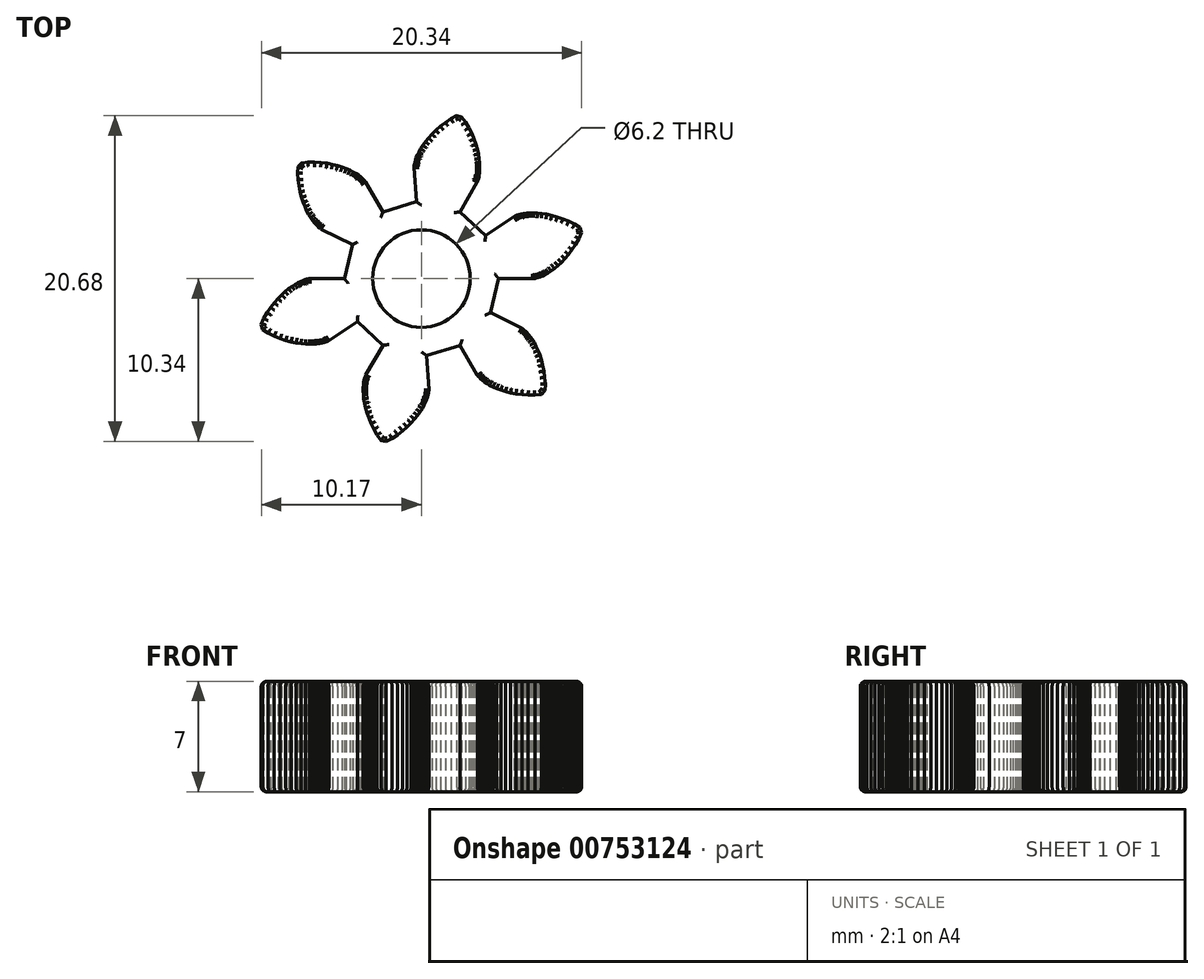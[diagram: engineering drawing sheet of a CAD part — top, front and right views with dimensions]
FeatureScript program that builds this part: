
annotation { "Feature Type Name" : "Feature", "Feature Type Description" : "" }
export const myFeature = defineFeature(function(context is Context, id is Id, definition is map)
    precondition{}
    {
        {
            var Q0;
            Q0=qCreatedBy(makeId("Top.planeOp"),FACE);
            var sketch = newSketch(context, id + "F0", { "sketchPlane" : qUnion([Q0])});
            skLineSegment(sketch, "E0", {"start": v(4.9, 0) * mm, "end": v(7.07, 0) * mm});
            skLineSegment(sketch, "E1", {"start": v(7.07, 0) * mm, "end": v(7.1, 0) * mm});
            skLineSegment(sketch, "E2", {"start": v(7.1, 0) * mm, "end": v(7.14, 0) * mm});
            skLineSegment(sketch, "E3", {"start": v(7.14, 0) * mm, "end": v(7.2, 0.02) * mm});
            skLineSegment(sketch, "E4", {"start": v(7.2, 0.02) * mm, "end": v(7.29, 0.04) * mm});
            skLineSegment(sketch, "E5", {"start": v(7.29, 0.04) * mm, "end": v(7.4, 0.07) * mm});
            skLineSegment(sketch, "E6", {"start": v(7.4, 0.07) * mm, "end": v(7.53, 0.11) * mm});
            skLineSegment(sketch, "E7", {"start": v(7.53, 0.11) * mm, "end": v(7.68, 0.18) * mm});
            skLineSegment(sketch, "E8", {"start": v(7.68, 0.18) * mm, "end": v(7.85, 0.26) * mm});
            skLineSegment(sketch, "E9", {"start": v(7.85, 0.26) * mm, "end": v(8.03, 0.36) * mm});
            skLineSegment(sketch, "E10", {"start": v(8.03, 0.36) * mm, "end": v(8.23, 0.49) * mm});
            skLineSegment(sketch, "E11", {"start": v(8.23, 0.49) * mm, "end": v(8.44, 0.64) * mm});
            skLineSegment(sketch, "E12", {"start": v(8.44, 0.64) * mm, "end": v(8.66, 0.82) * mm});
            skLineSegment(sketch, "E13", {"start": v(8.66, 0.82) * mm, "end": v(8.88, 1.03) * mm});
            skLineSegment(sketch, "E14", {"start": v(8.88, 1.03) * mm, "end": v(9.11, 1.27) * mm});
            skLineSegment(sketch, "E15", {"start": v(9.11, 1.27) * mm, "end": v(9.34, 1.54) * mm});
            skLineSegment(sketch, "E16", {"start": v(9.34, 1.54) * mm, "end": v(9.57, 1.84) * mm});
            skLineSegment(sketch, "E17", {"start": v(9.57, 1.84) * mm, "end": v(9.8, 2.17) * mm});
            skLineSegment(sketch, "E18", {"start": v(9.8, 2.17) * mm, "end": v(10.01, 2.54) * mm});
            skLineSegment(sketch, "E19", {"start": v(10.01, 2.54) * mm, "end": v(10.17, 2.92) * mm});
            skLineSegment(sketch, "E20", {"start": v(10.17, 2.92) * mm, "end": v(10.08, 3.23) * mm});
            skLineSegment(sketch, "E21", {"start": v(10.08, 3.23) * mm, "end": v(9.73, 3.46) * mm});
            skLineSegment(sketch, "E22", {"start": v(9.73, 3.46) * mm, "end": v(9.35, 3.64) * mm});
            skLineSegment(sketch, "E23", {"start": v(9.35, 3.64) * mm, "end": v(8.98, 3.8) * mm});
            skLineSegment(sketch, "E24", {"start": v(8.98, 3.8) * mm, "end": v(8.62, 3.92) * mm});
            skLineSegment(sketch, "E25", {"start": v(8.62, 3.92) * mm, "end": v(8.28, 4.02) * mm});
            skLineSegment(sketch, "E26", {"start": v(8.28, 4.02) * mm, "end": v(7.95, 4.08) * mm});
            skLineSegment(sketch, "E27", {"start": v(7.95, 4.08) * mm, "end": v(7.65, 4.13) * mm});
            skLineSegment(sketch, "E28", {"start": v(7.65, 4.13) * mm, "end": v(7.37, 4.16) * mm});
            skLineSegment(sketch, "E29", {"start": v(7.37, 4.16) * mm, "end": v(7.11, 4.17) * mm});
            skLineSegment(sketch, "E30", {"start": v(7.11, 4.17) * mm, "end": v(6.88, 4.17) * mm});
            skLineSegment(sketch, "E31", {"start": v(6.88, 4.17) * mm, "end": v(6.67, 4.15) * mm});
            skLineSegment(sketch, "E32", {"start": v(6.67, 4.15) * mm, "end": v(6.48, 4.12) * mm});
            skLineSegment(sketch, "E33", {"start": v(6.48, 4.12) * mm, "end": v(6.32, 4.1) * mm});
            skLineSegment(sketch, "E34", {"start": v(6.32, 4.1) * mm, "end": v(6.19, 4.06) * mm});
            skLineSegment(sketch, "E35", {"start": v(6.19, 4.06) * mm, "end": v(6.08, 4.02) * mm});
            skLineSegment(sketch, "E36", {"start": v(6.08, 4.02) * mm, "end": v(6, 4) * mm});
            skLineSegment(sketch, "E37", {"start": v(6, 4) * mm, "end": v(5.93, 3.96) * mm});
            skLineSegment(sketch, "E38", {"start": v(5.93, 3.96) * mm, "end": v(5.9, 3.94) * mm});
            skLineSegment(sketch, "E39", {"start": v(5.9, 3.94) * mm, "end": v(5.88, 3.93) * mm});
            skLineSegment(sketch, "E40", {"start": v(5.88, 3.93) * mm, "end": v(4.07, 2.72) * mm});
            skLineSegment(sketch, "E41", {"start": v(4.07, 2.72) * mm, "end": v(2.45, 4.24) * mm});
            skLineSegment(sketch, "E42", {"start": v(2.45, 4.24) * mm, "end": v(3.54, 6.13) * mm});
            skLineSegment(sketch, "E43", {"start": v(3.54, 6.13) * mm, "end": v(3.55, 6.14) * mm});
            skLineSegment(sketch, "E44", {"start": v(3.55, 6.14) * mm, "end": v(3.56, 6.18) * mm});
            skLineSegment(sketch, "E45", {"start": v(3.56, 6.18) * mm, "end": v(3.59, 6.25) * mm});
            skLineSegment(sketch, "E46", {"start": v(3.59, 6.25) * mm, "end": v(3.61, 6.33) * mm});
            skLineSegment(sketch, "E47", {"start": v(3.61, 6.33) * mm, "end": v(3.64, 6.44) * mm});
            skLineSegment(sketch, "E48", {"start": v(3.64, 6.44) * mm, "end": v(3.67, 6.58) * mm});
            skLineSegment(sketch, "E49", {"start": v(3.67, 6.58) * mm, "end": v(3.69, 6.74) * mm});
            skLineSegment(sketch, "E50", {"start": v(3.69, 6.74) * mm, "end": v(3.7, 6.93) * mm});
            skLineSegment(sketch, "E51", {"start": v(3.7, 6.93) * mm, "end": v(3.7, 7.14) * mm});
            skLineSegment(sketch, "E52", {"start": v(3.7, 7.14) * mm, "end": v(3.7, 7.37) * mm});
            skLineSegment(sketch, "E53", {"start": v(3.7, 7.37) * mm, "end": v(3.66, 7.63) * mm});
            skLineSegment(sketch, "E54", {"start": v(3.66, 7.63) * mm, "end": v(3.62, 7.9) * mm});
            skLineSegment(sketch, "E55", {"start": v(3.62, 7.9) * mm, "end": v(3.55, 8.2) * mm});
            skLineSegment(sketch, "E56", {"start": v(3.55, 8.2) * mm, "end": v(3.46, 8.52) * mm});
            skLineSegment(sketch, "E57", {"start": v(3.46, 8.52) * mm, "end": v(3.34, 8.86) * mm});
            skLineSegment(sketch, "E58", {"start": v(3.34, 8.86) * mm, "end": v(3.2, 9.2) * mm});
            skLineSegment(sketch, "E59", {"start": v(3.2, 9.2) * mm, "end": v(3.02, 9.57) * mm});
            skLineSegment(sketch, "E60", {"start": v(3.02, 9.57) * mm, "end": v(2.81, 9.94) * mm});
            skLineSegment(sketch, "E61", {"start": v(2.81, 9.94) * mm, "end": v(2.56, 10.27) * mm});
            skLineSegment(sketch, "E62", {"start": v(2.56, 10.27) * mm, "end": v(2.24, 10.34) * mm});
            skLineSegment(sketch, "E63", {"start": v(2.24, 10.34) * mm, "end": v(1.87, 10.16) * mm});
            skLineSegment(sketch, "E64", {"start": v(1.87, 10.16) * mm, "end": v(1.52, 9.92) * mm});
            skLineSegment(sketch, "E65", {"start": v(1.52, 9.92) * mm, "end": v(1.2, 9.67) * mm});
            skLineSegment(sketch, "E66", {"start": v(1.2, 9.67) * mm, "end": v(0.92, 9.42) * mm});
            skLineSegment(sketch, "E67", {"start": v(0.92, 9.42) * mm, "end": v(0.66, 9.18) * mm});
            skLineSegment(sketch, "E68", {"start": v(0.66, 9.18) * mm, "end": v(0.44, 8.93) * mm});
            skLineSegment(sketch, "E69", {"start": v(0.44, 8.93) * mm, "end": v(0.25, 8.7) * mm});
            skLineSegment(sketch, "E70", {"start": v(0.25, 8.7) * mm, "end": v(0.08, 8.46) * mm});
            skLineSegment(sketch, "E71", {"start": v(0.08, 8.46) * mm, "end": v(-0.06, 8.24) * mm});
            skLineSegment(sketch, "E72", {"start": v(-0.06, 8.24) * mm, "end": v(-0.17, 8.04) * mm});
            skLineSegment(sketch, "E73", {"start": v(-0.17, 8.04) * mm, "end": v(-0.26, 7.85) * mm});
            skLineSegment(sketch, "E74", {"start": v(-0.26, 7.85) * mm, "end": v(-0.33, 7.68) * mm});
            skLineSegment(sketch, "E75", {"start": v(-0.33, 7.68) * mm, "end": v(-0.38, 7.52) * mm});
            skLineSegment(sketch, "E76", {"start": v(-0.38, 7.52) * mm, "end": v(-0.42, 7.39) * mm});
            skLineSegment(sketch, "E77", {"start": v(-0.42, 7.39) * mm, "end": v(-0.45, 7.28) * mm});
            skLineSegment(sketch, "E78", {"start": v(-0.45, 7.28) * mm, "end": v(-0.46, 7.19) * mm});
            skLineSegment(sketch, "E79", {"start": v(-0.46, 7.19) * mm, "end": v(-0.47, 7.12) * mm});
            skLineSegment(sketch, "E80", {"start": v(-0.47, 7.12) * mm, "end": v(-0.47, 7.08) * mm});
            skLineSegment(sketch, "E81", {"start": v(-0.47, 7.08) * mm, "end": v(-0.47, 7.06) * mm});
            skLineSegment(sketch, "E82", {"start": v(-0.47, 7.06) * mm, "end": v(-0.32, 4.88) * mm});
            skLineSegment(sketch, "E83", {"start": v(-0.32, 4.88) * mm, "end": v(-2.45, 4.24) * mm});
            skLineSegment(sketch, "E84", {"start": v(-2.45, 4.24) * mm, "end": v(-3.54, 6.13) * mm});
            skLineSegment(sketch, "E85", {"start": v(-3.54, 6.13) * mm, "end": v(-3.55, 6.14) * mm});
            skLineSegment(sketch, "E86", {"start": v(-3.55, 6.14) * mm, "end": v(-3.57, 6.18) * mm});
            skLineSegment(sketch, "E87", {"start": v(-3.57, 6.18) * mm, "end": v(-3.61, 6.23) * mm});
            skLineSegment(sketch, "E88", {"start": v(-3.61, 6.23) * mm, "end": v(-3.68, 6.3) * mm});
            skLineSegment(sketch, "E89", {"start": v(-3.68, 6.3) * mm, "end": v(-3.76, 6.37) * mm});
            skLineSegment(sketch, "E90", {"start": v(-3.76, 6.37) * mm, "end": v(-3.87, 6.47) * mm});
            skLineSegment(sketch, "E91", {"start": v(-3.87, 6.47) * mm, "end": v(-4, 6.56) * mm});
            skLineSegment(sketch, "E92", {"start": v(-4, 6.56) * mm, "end": v(-4.15, 6.67) * mm});
            skLineSegment(sketch, "E93", {"start": v(-4.15, 6.67) * mm, "end": v(-4.33, 6.78) * mm});
            skLineSegment(sketch, "E94", {"start": v(-4.33, 6.78) * mm, "end": v(-4.54, 6.88) * mm});
            skLineSegment(sketch, "E95", {"start": v(-4.54, 6.88) * mm, "end": v(-4.77, 6.99) * mm});
            skLineSegment(sketch, "E96", {"start": v(-4.77, 6.99) * mm, "end": v(-5.04, 7.09) * mm});
            skLineSegment(sketch, "E97", {"start": v(-5.04, 7.09) * mm, "end": v(-5.33, 7.18) * mm});
            skLineSegment(sketch, "E98", {"start": v(-5.33, 7.18) * mm, "end": v(-5.65, 7.26) * mm});
            skLineSegment(sketch, "E99", {"start": v(-5.65, 7.26) * mm, "end": v(-6, 7.32) * mm});
            skLineSegment(sketch, "E100", {"start": v(-6, 7.32) * mm, "end": v(-6.38, 7.37) * mm});
            skLineSegment(sketch, "E101", {"start": v(-6.38, 7.37) * mm, "end": v(-6.78, 7.4) * mm});
            skLineSegment(sketch, "E102", {"start": v(-6.78, 7.4) * mm, "end": v(-7.2, 7.4) * mm});
            skLineSegment(sketch, "E103", {"start": v(-7.2, 7.4) * mm, "end": v(-7.62, 7.35) * mm});
            skLineSegment(sketch, "E104", {"start": v(-7.62, 7.35) * mm, "end": v(-7.84, 7.11) * mm});
            skLineSegment(sketch, "E105", {"start": v(-7.84, 7.11) * mm, "end": v(-7.86, 6.7) * mm});
            skLineSegment(sketch, "E106", {"start": v(-7.86, 6.7) * mm, "end": v(-7.83, 6.27) * mm});
            skLineSegment(sketch, "E107", {"start": v(-7.83, 6.27) * mm, "end": v(-7.78, 5.87) * mm});
            skLineSegment(sketch, "E108", {"start": v(-7.78, 5.87) * mm, "end": v(-7.7, 5.5) * mm});
            skLineSegment(sketch, "E109", {"start": v(-7.7, 5.5) * mm, "end": v(-7.62, 5.16) * mm});
            skLineSegment(sketch, "E110", {"start": v(-7.62, 5.16) * mm, "end": v(-7.51, 4.85) * mm});
            skLineSegment(sketch, "E111", {"start": v(-7.51, 4.85) * mm, "end": v(-7.4, 4.56) * mm});
            skLineSegment(sketch, "E112", {"start": v(-7.4, 4.56) * mm, "end": v(-7.29, 4.3) * mm});
            skLineSegment(sketch, "E113", {"start": v(-7.29, 4.3) * mm, "end": v(-7.17, 4.07) * mm});
            skLineSegment(sketch, "E114", {"start": v(-7.17, 4.07) * mm, "end": v(-7.05, 3.87) * mm});
            skLineSegment(sketch, "E115", {"start": v(-7.05, 3.87) * mm, "end": v(-6.93, 3.7) * mm});
            skLineSegment(sketch, "E116", {"start": v(-6.93, 3.7) * mm, "end": v(-6.81, 3.55) * mm});
            skLineSegment(sketch, "E117", {"start": v(-6.81, 3.55) * mm, "end": v(-6.7, 3.43) * mm});
            skLineSegment(sketch, "E118", {"start": v(-6.7, 3.43) * mm, "end": v(-6.6, 3.33) * mm});
            skLineSegment(sketch, "E119", {"start": v(-6.6, 3.33) * mm, "end": v(-6.52, 3.25) * mm});
            skLineSegment(sketch, "E120", {"start": v(-6.52, 3.25) * mm, "end": v(-6.45, 3.2) * mm});
            skLineSegment(sketch, "E121", {"start": v(-6.45, 3.2) * mm, "end": v(-6.4, 3.16) * mm});
            skLineSegment(sketch, "E122", {"start": v(-6.4, 3.16) * mm, "end": v(-6.36, 3.13) * mm});
            skLineSegment(sketch, "E123", {"start": v(-6.36, 3.13) * mm, "end": v(-6.35, 3.13) * mm});
            skLineSegment(sketch, "E124", {"start": v(-6.35, 3.13) * mm, "end": v(-4.4, 2.16) * mm});
            skLineSegment(sketch, "E125", {"start": v(-4.4, 2.16) * mm, "end": v(-4.9, 0) * mm});
            skLineSegment(sketch, "E126", {"start": v(-4.9, 0) * mm, "end": v(-7.07, 0) * mm});
            skLineSegment(sketch, "E127", {"start": v(-7.07, 0) * mm, "end": v(-7.1, 0) * mm});
            skLineSegment(sketch, "E128", {"start": v(-7.1, 0) * mm, "end": v(-7.14, 0) * mm});
            skLineSegment(sketch, "E129", {"start": v(-7.14, 0) * mm, "end": v(-7.2, -0.02) * mm});
            skLineSegment(sketch, "E130", {"start": v(-7.2, -0.02) * mm, "end": v(-7.29, -0.04) * mm});
            skLineSegment(sketch, "E131", {"start": v(-7.29, -0.04) * mm, "end": v(-7.4, -0.07) * mm});
            skLineSegment(sketch, "E132", {"start": v(-7.4, -0.07) * mm, "end": v(-7.53, -0.11) * mm});
            skLineSegment(sketch, "E133", {"start": v(-7.53, -0.11) * mm, "end": v(-7.68, -0.18) * mm});
            skLineSegment(sketch, "E134", {"start": v(-7.68, -0.18) * mm, "end": v(-7.85, -0.26) * mm});
            skLineSegment(sketch, "E135", {"start": v(-7.85, -0.26) * mm, "end": v(-8.03, -0.36) * mm});
            skLineSegment(sketch, "E136", {"start": v(-8.03, -0.36) * mm, "end": v(-8.23, -0.49) * mm});
            skLineSegment(sketch, "E137", {"start": v(-8.23, -0.49) * mm, "end": v(-8.44, -0.64) * mm});
            skLineSegment(sketch, "E138", {"start": v(-8.44, -0.64) * mm, "end": v(-8.66, -0.82) * mm});
            skLineSegment(sketch, "E139", {"start": v(-8.66, -0.82) * mm, "end": v(-8.88, -1.03) * mm});
            skLineSegment(sketch, "E140", {"start": v(-8.88, -1.03) * mm, "end": v(-9.11, -1.27) * mm});
            skLineSegment(sketch, "E141", {"start": v(-9.11, -1.27) * mm, "end": v(-9.34, -1.54) * mm});
            skLineSegment(sketch, "E142", {"start": v(-9.34, -1.54) * mm, "end": v(-9.57, -1.84) * mm});
            skLineSegment(sketch, "E143", {"start": v(-9.57, -1.84) * mm, "end": v(-9.8, -2.17) * mm});
            skLineSegment(sketch, "E144", {"start": v(-9.8, -2.17) * mm, "end": v(-10.01, -2.54) * mm});
            skLineSegment(sketch, "E145", {"start": v(-10.01, -2.54) * mm, "end": v(-10.17, -2.92) * mm});
            skLineSegment(sketch, "E146", {"start": v(-10.17, -2.92) * mm, "end": v(-10.08, -3.23) * mm});
            skLineSegment(sketch, "E147", {"start": v(-10.08, -3.23) * mm, "end": v(-9.73, -3.46) * mm});
            skLineSegment(sketch, "E148", {"start": v(-9.73, -3.46) * mm, "end": v(-9.35, -3.64) * mm});
            skLineSegment(sketch, "E149", {"start": v(-9.35, -3.64) * mm, "end": v(-8.98, -3.8) * mm});
            skLineSegment(sketch, "E150", {"start": v(-8.98, -3.8) * mm, "end": v(-8.62, -3.92) * mm});
            skLineSegment(sketch, "E151", {"start": v(-8.62, -3.92) * mm, "end": v(-8.28, -4.02) * mm});
            skLineSegment(sketch, "E152", {"start": v(-8.28, -4.02) * mm, "end": v(-7.95, -4.08) * mm});
            skLineSegment(sketch, "E153", {"start": v(-7.95, -4.08) * mm, "end": v(-7.65, -4.13) * mm});
            skLineSegment(sketch, "E154", {"start": v(-7.65, -4.13) * mm, "end": v(-7.37, -4.16) * mm});
            skLineSegment(sketch, "E155", {"start": v(-7.37, -4.16) * mm, "end": v(-7.11, -4.17) * mm});
            skLineSegment(sketch, "E156", {"start": v(-7.11, -4.17) * mm, "end": v(-6.88, -4.17) * mm});
            skLineSegment(sketch, "E157", {"start": v(-6.88, -4.17) * mm, "end": v(-6.67, -4.15) * mm});
            skLineSegment(sketch, "E158", {"start": v(-6.67, -4.15) * mm, "end": v(-6.48, -4.12) * mm});
            skLineSegment(sketch, "E159", {"start": v(-6.48, -4.12) * mm, "end": v(-6.32, -4.1) * mm});
            skLineSegment(sketch, "E160", {"start": v(-6.32, -4.1) * mm, "end": v(-6.19, -4.06) * mm});
            skLineSegment(sketch, "E161", {"start": v(-6.19, -4.06) * mm, "end": v(-6.08, -4.02) * mm});
            skLineSegment(sketch, "E162", {"start": v(-6.08, -4.02) * mm, "end": v(-6, -4) * mm});
            skLineSegment(sketch, "E163", {"start": v(-6, -4) * mm, "end": v(-5.93, -3.96) * mm});
            skLineSegment(sketch, "E164", {"start": v(-5.93, -3.96) * mm, "end": v(-5.9, -3.94) * mm});
            skLineSegment(sketch, "E165", {"start": v(-5.9, -3.94) * mm, "end": v(-5.88, -3.93) * mm});
            skLineSegment(sketch, "E166", {"start": v(-5.88, -3.93) * mm, "end": v(-4.07, -2.72) * mm});
            skLineSegment(sketch, "E167", {"start": v(-4.07, -2.72) * mm, "end": v(-2.45, -4.24) * mm});
            skLineSegment(sketch, "E168", {"start": v(-2.45, -4.24) * mm, "end": v(-3.54, -6.13) * mm});
            skLineSegment(sketch, "E169", {"start": v(-3.54, -6.13) * mm, "end": v(-3.55, -6.14) * mm});
            skLineSegment(sketch, "E170", {"start": v(-3.55, -6.14) * mm, "end": v(-3.56, -6.18) * mm});
            skLineSegment(sketch, "E171", {"start": v(-3.56, -6.18) * mm, "end": v(-3.59, -6.25) * mm});
            skLineSegment(sketch, "E172", {"start": v(-3.59, -6.25) * mm, "end": v(-3.61, -6.33) * mm});
            skLineSegment(sketch, "E173", {"start": v(-3.61, -6.33) * mm, "end": v(-3.64, -6.44) * mm});
            skLineSegment(sketch, "E174", {"start": v(-3.64, -6.44) * mm, "end": v(-3.67, -6.58) * mm});
            skLineSegment(sketch, "E175", {"start": v(-3.67, -6.58) * mm, "end": v(-3.69, -6.74) * mm});
            skLineSegment(sketch, "E176", {"start": v(-3.69, -6.74) * mm, "end": v(-3.7, -6.93) * mm});
            skLineSegment(sketch, "E177", {"start": v(-3.7, -6.93) * mm, "end": v(-3.7, -7.14) * mm});
            skLineSegment(sketch, "E178", {"start": v(-3.7, -7.14) * mm, "end": v(-3.7, -7.37) * mm});
            skLineSegment(sketch, "E179", {"start": v(-3.7, -7.37) * mm, "end": v(-3.66, -7.63) * mm});
            skLineSegment(sketch, "E180", {"start": v(-3.66, -7.63) * mm, "end": v(-3.62, -7.9) * mm});
            skLineSegment(sketch, "E181", {"start": v(-3.62, -7.9) * mm, "end": v(-3.55, -8.2) * mm});
            skLineSegment(sketch, "E182", {"start": v(-3.55, -8.2) * mm, "end": v(-3.46, -8.52) * mm});
            skLineSegment(sketch, "E183", {"start": v(-3.46, -8.52) * mm, "end": v(-3.34, -8.86) * mm});
            skLineSegment(sketch, "E184", {"start": v(-3.34, -8.86) * mm, "end": v(-3.2, -9.2) * mm});
            skLineSegment(sketch, "E185", {"start": v(-3.2, -9.2) * mm, "end": v(-3.02, -9.57) * mm});
            skLineSegment(sketch, "E186", {"start": v(-3.02, -9.57) * mm, "end": v(-2.81, -9.94) * mm});
            skLineSegment(sketch, "E187", {"start": v(-2.81, -9.94) * mm, "end": v(-2.56, -10.27) * mm});
            skLineSegment(sketch, "E188", {"start": v(-2.56, -10.27) * mm, "end": v(-2.24, -10.34) * mm});
            skLineSegment(sketch, "E189", {"start": v(-2.24, -10.34) * mm, "end": v(-1.87, -10.16) * mm});
            skLineSegment(sketch, "E190", {"start": v(-1.87, -10.16) * mm, "end": v(-1.52, -9.92) * mm});
            skLineSegment(sketch, "E191", {"start": v(-1.52, -9.92) * mm, "end": v(-1.2, -9.67) * mm});
            skLineSegment(sketch, "E192", {"start": v(-1.2, -9.67) * mm, "end": v(-0.91, -9.42) * mm});
            skLineSegment(sketch, "E193", {"start": v(-0.91, -9.42) * mm, "end": v(-0.66, -9.18) * mm});
            skLineSegment(sketch, "E194", {"start": v(-0.66, -9.18) * mm, "end": v(-0.44, -8.93) * mm});
            skLineSegment(sketch, "E195", {"start": v(-0.44, -8.93) * mm, "end": v(-0.25, -8.7) * mm});
            skLineSegment(sketch, "E196", {"start": v(-0.25, -8.7) * mm, "end": v(-0.08, -8.46) * mm});
            skLineSegment(sketch, "E197", {"start": v(-0.08, -8.46) * mm, "end": v(0.06, -8.24) * mm});
            skLineSegment(sketch, "E198", {"start": v(0.06, -8.24) * mm, "end": v(0.17, -8.04) * mm});
            skLineSegment(sketch, "E199", {"start": v(0.17, -8.04) * mm, "end": v(0.26, -7.85) * mm});
            skLineSegment(sketch, "E200", {"start": v(0.26, -7.85) * mm, "end": v(0.33, -7.68) * mm});
            skLineSegment(sketch, "E201", {"start": v(0.33, -7.68) * mm, "end": v(0.38, -7.52) * mm});
            skLineSegment(sketch, "E202", {"start": v(0.38, -7.52) * mm, "end": v(0.42, -7.39) * mm});
            skLineSegment(sketch, "E203", {"start": v(0.42, -7.39) * mm, "end": v(0.45, -7.28) * mm});
            skLineSegment(sketch, "E204", {"start": v(0.45, -7.28) * mm, "end": v(0.46, -7.19) * mm});
            skLineSegment(sketch, "E205", {"start": v(0.46, -7.19) * mm, "end": v(0.47, -7.12) * mm});
            skLineSegment(sketch, "E206", {"start": v(0.47, -7.12) * mm, "end": v(0.47, -7.08) * mm});
            skLineSegment(sketch, "E207", {"start": v(0.47, -7.08) * mm, "end": v(0.47, -7.06) * mm});
            skLineSegment(sketch, "E208", {"start": v(0.47, -7.06) * mm, "end": v(0.32, -4.88) * mm});
            skLineSegment(sketch, "E209", {"start": v(0.32, -4.88) * mm, "end": v(2.45, -4.24) * mm});
            skLineSegment(sketch, "E210", {"start": v(2.45, -4.24) * mm, "end": v(3.54, -6.13) * mm});
            skLineSegment(sketch, "E211", {"start": v(3.54, -6.13) * mm, "end": v(3.55, -6.14) * mm});
            skLineSegment(sketch, "E212", {"start": v(3.55, -6.14) * mm, "end": v(3.57, -6.18) * mm});
            skLineSegment(sketch, "E213", {"start": v(3.57, -6.18) * mm, "end": v(3.61, -6.23) * mm});
            skLineSegment(sketch, "E214", {"start": v(3.61, -6.23) * mm, "end": v(3.68, -6.3) * mm});
            skLineSegment(sketch, "E215", {"start": v(3.68, -6.3) * mm, "end": v(3.76, -6.37) * mm});
            skLineSegment(sketch, "E216", {"start": v(3.76, -6.37) * mm, "end": v(3.87, -6.47) * mm});
            skLineSegment(sketch, "E217", {"start": v(3.87, -6.47) * mm, "end": v(4, -6.56) * mm});
            skLineSegment(sketch, "E218", {"start": v(4, -6.56) * mm, "end": v(4.15, -6.67) * mm});
            skLineSegment(sketch, "E219", {"start": v(4.15, -6.67) * mm, "end": v(4.33, -6.78) * mm});
            skLineSegment(sketch, "E220", {"start": v(4.33, -6.78) * mm, "end": v(4.54, -6.88) * mm});
            skLineSegment(sketch, "E221", {"start": v(4.54, -6.88) * mm, "end": v(4.77, -6.99) * mm});
            skLineSegment(sketch, "E222", {"start": v(4.77, -6.99) * mm, "end": v(5.04, -7.09) * mm});
            skLineSegment(sketch, "E223", {"start": v(5.04, -7.09) * mm, "end": v(5.33, -7.18) * mm});
            skLineSegment(sketch, "E224", {"start": v(5.33, -7.18) * mm, "end": v(5.65, -7.26) * mm});
            skLineSegment(sketch, "E225", {"start": v(5.65, -7.26) * mm, "end": v(6, -7.32) * mm});
            skLineSegment(sketch, "E226", {"start": v(6, -7.32) * mm, "end": v(6.38, -7.37) * mm});
            skLineSegment(sketch, "E227", {"start": v(6.38, -7.37) * mm, "end": v(6.78, -7.4) * mm});
            skLineSegment(sketch, "E228", {"start": v(6.78, -7.4) * mm, "end": v(7.2, -7.4) * mm});
            skLineSegment(sketch, "E229", {"start": v(7.2, -7.4) * mm, "end": v(7.62, -7.35) * mm});
            skLineSegment(sketch, "E230", {"start": v(7.62, -7.35) * mm, "end": v(7.84, -7.11) * mm});
            skLineSegment(sketch, "E231", {"start": v(7.84, -7.11) * mm, "end": v(7.86, -6.7) * mm});
            skLineSegment(sketch, "E232", {"start": v(7.86, -6.7) * mm, "end": v(7.83, -6.27) * mm});
            skLineSegment(sketch, "E233", {"start": v(7.83, -6.27) * mm, "end": v(7.78, -5.87) * mm});
            skLineSegment(sketch, "E234", {"start": v(7.78, -5.87) * mm, "end": v(7.7, -5.5) * mm});
            skLineSegment(sketch, "E235", {"start": v(7.7, -5.5) * mm, "end": v(7.62, -5.16) * mm});
            skLineSegment(sketch, "E236", {"start": v(7.62, -5.16) * mm, "end": v(7.51, -4.85) * mm});
            skLineSegment(sketch, "E237", {"start": v(7.51, -4.85) * mm, "end": v(7.4, -4.56) * mm});
            skLineSegment(sketch, "E238", {"start": v(7.4, -4.56) * mm, "end": v(7.29, -4.3) * mm});
            skLineSegment(sketch, "E239", {"start": v(7.29, -4.3) * mm, "end": v(7.17, -4.07) * mm});
            skLineSegment(sketch, "E240", {"start": v(7.17, -4.07) * mm, "end": v(7.05, -3.87) * mm});
            skLineSegment(sketch, "E241", {"start": v(7.05, -3.87) * mm, "end": v(6.93, -3.7) * mm});
            skLineSegment(sketch, "E242", {"start": v(6.93, -3.7) * mm, "end": v(6.81, -3.55) * mm});
            skLineSegment(sketch, "E243", {"start": v(6.81, -3.55) * mm, "end": v(6.7, -3.43) * mm});
            skLineSegment(sketch, "E244", {"start": v(6.7, -3.43) * mm, "end": v(6.6, -3.33) * mm});
            skLineSegment(sketch, "E245", {"start": v(6.6, -3.33) * mm, "end": v(6.52, -3.25) * mm});
            skLineSegment(sketch, "E246", {"start": v(6.52, -3.25) * mm, "end": v(6.45, -3.2) * mm});
            skLineSegment(sketch, "E247", {"start": v(6.45, -3.2) * mm, "end": v(6.4, -3.16) * mm});
            skLineSegment(sketch, "E248", {"start": v(6.4, -3.16) * mm, "end": v(6.36, -3.13) * mm});
            skLineSegment(sketch, "E249", {"start": v(6.36, -3.13) * mm, "end": v(6.35, -3.13) * mm});
            skLineSegment(sketch, "E250", {"start": v(6.35, -3.13) * mm, "end": v(4.4, -2.16) * mm});
            skLineSegment(sketch, "E251", {"start": v(4.4, -2.16) * mm, "end": v(4.9, 0) * mm});
            skCircle(sketch, "E252", {"center": v(0, 0) * mm, "radius": 3.1 * mm});
            skSolve(sketch);
        }
        {
            var Q0;
            Q0 = qSketchRegion(id + "F0", true);
            extrude(context, id + "F1", {"entities" : qUnion([Q0]), "depth" : 7 * mm, "offsetDistance" : 25 * mm});
        }
        {
            var Q0;
            Q0=makeQuery(id+"F1.opExtrude","CAP_FACE",FACE,{"disambiguationData":[OSD([sQuery(id+"F0.wireOp",EDGE,"E0"),sQuery(id+"F0.wireOp",EDGE,"E1"),sQuery(id+"F0.wireOp",EDGE,"E2"),sQuery(id+"F0.wireOp",EDGE,"E3"),sQuery(id+"F0.wireOp",EDGE,"E4"),sQuery(id+"F0.wireOp",EDGE,"E5"),sQuery(id+"F0.wireOp",EDGE,"E6"),sQuery(id+"F0.wireOp",EDGE,"E7"),sQuery(id+"F0.wireOp",EDGE,"E8"),sQuery(id+"F0.wireOp",EDGE,"E9"),sQuery(id+"F0.wireOp",EDGE,"E10"),sQuery(id+"F0.wireOp",EDGE,"E11"),sQuery(id+"F0.wireOp",EDGE,"E12"),sQuery(id+"F0.wireOp",EDGE,"E13"),sQuery(id+"F0.wireOp",EDGE,"E14"),sQuery(id+"F0.wireOp",EDGE,"E15"),sQuery(id+"F0.wireOp",EDGE,"E16"),sQuery(id+"F0.wireOp",EDGE,"E17"),sQuery(id+"F0.wireOp",EDGE,"E18"),sQuery(id+"F0.wireOp",EDGE,"E19"),sQuery(id+"F0.wireOp",EDGE,"E20"),sQuery(id+"F0.wireOp",EDGE,"E21"),sQuery(id+"F0.wireOp",EDGE,"E22"),sQuery(id+"F0.wireOp",EDGE,"E23"),sQuery(id+"F0.wireOp",EDGE,"E24"),sQuery(id+"F0.wireOp",EDGE,"E25"),sQuery(id+"F0.wireOp",EDGE,"E26"),sQuery(id+"F0.wireOp",EDGE,"E27"),sQuery(id+"F0.wireOp",EDGE,"E28"),sQuery(id+"F0.wireOp",EDGE,"E29"),sQuery(id+"F0.wireOp",EDGE,"E30"),sQuery(id+"F0.wireOp",EDGE,"E31"),sQuery(id+"F0.wireOp",EDGE,"E32"),sQuery(id+"F0.wireOp",EDGE,"E33"),sQuery(id+"F0.wireOp",EDGE,"E34"),sQuery(id+"F0.wireOp",EDGE,"E35"),sQuery(id+"F0.wireOp",EDGE,"E36"),sQuery(id+"F0.wireOp",EDGE,"E37"),sQuery(id+"F0.wireOp",EDGE,"E38"),sQuery(id+"F0.wireOp",EDGE,"E39"),sQuery(id+"F0.wireOp",EDGE,"E40"),sQuery(id+"F0.wireOp",EDGE,"E41"),sQuery(id+"F0.wireOp",EDGE,"E42"),sQuery(id+"F0.wireOp",EDGE,"E43"),sQuery(id+"F0.wireOp",EDGE,"E44"),sQuery(id+"F0.wireOp",EDGE,"E45"),sQuery(id+"F0.wireOp",EDGE,"E46"),sQuery(id+"F0.wireOp",EDGE,"E47"),sQuery(id+"F0.wireOp",EDGE,"E48"),sQuery(id+"F0.wireOp",EDGE,"E49"),sQuery(id+"F0.wireOp",EDGE,"E50"),sQuery(id+"F0.wireOp",EDGE,"E51"),sQuery(id+"F0.wireOp",EDGE,"E52"),sQuery(id+"F0.wireOp",EDGE,"E53"),sQuery(id+"F0.wireOp",EDGE,"E54"),sQuery(id+"F0.wireOp",EDGE,"E55"),sQuery(id+"F0.wireOp",EDGE,"E56"),sQuery(id+"F0.wireOp",EDGE,"E57"),sQuery(id+"F0.wireOp",EDGE,"E58"),sQuery(id+"F0.wireOp",EDGE,"E59"),sQuery(id+"F0.wireOp",EDGE,"E60"),sQuery(id+"F0.wireOp",EDGE,"E61"),sQuery(id+"F0.wireOp",EDGE,"E62"),sQuery(id+"F0.wireOp",EDGE,"E63"),sQuery(id+"F0.wireOp",EDGE,"E64"),sQuery(id+"F0.wireOp",EDGE,"E65"),sQuery(id+"F0.wireOp",EDGE,"E66"),sQuery(id+"F0.wireOp",EDGE,"E67"),sQuery(id+"F0.wireOp",EDGE,"E68"),sQuery(id+"F0.wireOp",EDGE,"E69"),sQuery(id+"F0.wireOp",EDGE,"E70"),sQuery(id+"F0.wireOp",EDGE,"E71"),sQuery(id+"F0.wireOp",EDGE,"E72"),sQuery(id+"F0.wireOp",EDGE,"E73"),sQuery(id+"F0.wireOp",EDGE,"E74"),sQuery(id+"F0.wireOp",EDGE,"E75"),sQuery(id+"F0.wireOp",EDGE,"E76"),sQuery(id+"F0.wireOp",EDGE,"E77"),sQuery(id+"F0.wireOp",EDGE,"E78"),sQuery(id+"F0.wireOp",EDGE,"E79"),sQuery(id+"F0.wireOp",EDGE,"E80"),sQuery(id+"F0.wireOp",EDGE,"E81"),sQuery(id+"F0.wireOp",EDGE,"E82"),sQuery(id+"F0.wireOp",EDGE,"E83"),sQuery(id+"F0.wireOp",EDGE,"E84"),sQuery(id+"F0.wireOp",EDGE,"E85"),sQuery(id+"F0.wireOp",EDGE,"E86"),sQuery(id+"F0.wireOp",EDGE,"E87"),sQuery(id+"F0.wireOp",EDGE,"E88"),sQuery(id+"F0.wireOp",EDGE,"E89"),sQuery(id+"F0.wireOp",EDGE,"E90"),sQuery(id+"F0.wireOp",EDGE,"E91"),sQuery(id+"F0.wireOp",EDGE,"E92"),sQuery(id+"F0.wireOp",EDGE,"E93"),sQuery(id+"F0.wireOp",EDGE,"E94"),sQuery(id+"F0.wireOp",EDGE,"E95"),sQuery(id+"F0.wireOp",EDGE,"E96"),sQuery(id+"F0.wireOp",EDGE,"E97"),sQuery(id+"F0.wireOp",EDGE,"E98"),sQuery(id+"F0.wireOp",EDGE,"E99"),sQuery(id+"F0.wireOp",EDGE,"E100"),sQuery(id+"F0.wireOp",EDGE,"E101"),sQuery(id+"F0.wireOp",EDGE,"E102"),sQuery(id+"F0.wireOp",EDGE,"E103"),sQuery(id+"F0.wireOp",EDGE,"E104"),sQuery(id+"F0.wireOp",EDGE,"E105"),sQuery(id+"F0.wireOp",EDGE,"E106"),sQuery(id+"F0.wireOp",EDGE,"E107"),sQuery(id+"F0.wireOp",EDGE,"E108"),sQuery(id+"F0.wireOp",EDGE,"E109"),sQuery(id+"F0.wireOp",EDGE,"E110"),sQuery(id+"F0.wireOp",EDGE,"E111"),sQuery(id+"F0.wireOp",EDGE,"E112"),sQuery(id+"F0.wireOp",EDGE,"E113"),sQuery(id+"F0.wireOp",EDGE,"E114"),sQuery(id+"F0.wireOp",EDGE,"E115"),sQuery(id+"F0.wireOp",EDGE,"E116"),sQuery(id+"F0.wireOp",EDGE,"E117"),sQuery(id+"F0.wireOp",EDGE,"E118"),sQuery(id+"F0.wireOp",EDGE,"E119"),sQuery(id+"F0.wireOp",EDGE,"E120"),sQuery(id+"F0.wireOp",EDGE,"E121"),sQuery(id+"F0.wireOp",EDGE,"E122"),sQuery(id+"F0.wireOp",EDGE,"E123"),sQuery(id+"F0.wireOp",EDGE,"E124"),sQuery(id+"F0.wireOp",EDGE,"E125"),sQuery(id+"F0.wireOp",EDGE,"E126"),sQuery(id+"F0.wireOp",EDGE,"E127"),sQuery(id+"F0.wireOp",EDGE,"E128"),sQuery(id+"F0.wireOp",EDGE,"E129"),sQuery(id+"F0.wireOp",EDGE,"E130"),sQuery(id+"F0.wireOp",EDGE,"E131"),sQuery(id+"F0.wireOp",EDGE,"E132"),sQuery(id+"F0.wireOp",EDGE,"E133"),sQuery(id+"F0.wireOp",EDGE,"E134"),sQuery(id+"F0.wireOp",EDGE,"E135"),sQuery(id+"F0.wireOp",EDGE,"E136"),sQuery(id+"F0.wireOp",EDGE,"E137"),sQuery(id+"F0.wireOp",EDGE,"E138"),sQuery(id+"F0.wireOp",EDGE,"E139"),sQuery(id+"F0.wireOp",EDGE,"E140"),sQuery(id+"F0.wireOp",EDGE,"E141"),sQuery(id+"F0.wireOp",EDGE,"E142"),sQuery(id+"F0.wireOp",EDGE,"E143"),sQuery(id+"F0.wireOp",EDGE,"E144"),sQuery(id+"F0.wireOp",EDGE,"E145"),sQuery(id+"F0.wireOp",EDGE,"E146"),sQuery(id+"F0.wireOp",EDGE,"E147"),sQuery(id+"F0.wireOp",EDGE,"E148"),sQuery(id+"F0.wireOp",EDGE,"E149"),sQuery(id+"F0.wireOp",EDGE,"E150"),sQuery(id+"F0.wireOp",EDGE,"E151"),sQuery(id+"F0.wireOp",EDGE,"E152"),sQuery(id+"F0.wireOp",EDGE,"E153"),sQuery(id+"F0.wireOp",EDGE,"E154"),sQuery(id+"F0.wireOp",EDGE,"E155"),sQuery(id+"F0.wireOp",EDGE,"E156"),sQuery(id+"F0.wireOp",EDGE,"E157"),sQuery(id+"F0.wireOp",EDGE,"E158"),sQuery(id+"F0.wireOp",EDGE,"E159"),sQuery(id+"F0.wireOp",EDGE,"E160"),sQuery(id+"F0.wireOp",EDGE,"E161"),sQuery(id+"F0.wireOp",EDGE,"E162"),sQuery(id+"F0.wireOp",EDGE,"E163"),sQuery(id+"F0.wireOp",EDGE,"E164"),sQuery(id+"F0.wireOp",EDGE,"E165"),sQuery(id+"F0.wireOp",EDGE,"E166"),sQuery(id+"F0.wireOp",EDGE,"E167"),sQuery(id+"F0.wireOp",EDGE,"E168"),sQuery(id+"F0.wireOp",EDGE,"E169"),sQuery(id+"F0.wireOp",EDGE,"E170"),sQuery(id+"F0.wireOp",EDGE,"E171"),sQuery(id+"F0.wireOp",EDGE,"E172"),sQuery(id+"F0.wireOp",EDGE,"E173"),sQuery(id+"F0.wireOp",EDGE,"E174"),sQuery(id+"F0.wireOp",EDGE,"E175"),sQuery(id+"F0.wireOp",EDGE,"E176"),sQuery(id+"F0.wireOp",EDGE,"E177"),sQuery(id+"F0.wireOp",EDGE,"E178"),sQuery(id+"F0.wireOp",EDGE,"E179"),sQuery(id+"F0.wireOp",EDGE,"E180"),sQuery(id+"F0.wireOp",EDGE,"E181"),sQuery(id+"F0.wireOp",EDGE,"E182"),sQuery(id+"F0.wireOp",EDGE,"E183"),sQuery(id+"F0.wireOp",EDGE,"E184"),sQuery(id+"F0.wireOp",EDGE,"E185"),sQuery(id+"F0.wireOp",EDGE,"E186"),sQuery(id+"F0.wireOp",EDGE,"E187"),sQuery(id+"F0.wireOp",EDGE,"E188"),sQuery(id+"F0.wireOp",EDGE,"E189"),sQuery(id+"F0.wireOp",EDGE,"E190"),sQuery(id+"F0.wireOp",EDGE,"E191"),sQuery(id+"F0.wireOp",EDGE,"E192"),sQuery(id+"F0.wireOp",EDGE,"E193"),sQuery(id+"F0.wireOp",EDGE,"E194"),sQuery(id+"F0.wireOp",EDGE,"E195"),sQuery(id+"F0.wireOp",EDGE,"E196"),sQuery(id+"F0.wireOp",EDGE,"E197"),sQuery(id+"F0.wireOp",EDGE,"E198"),sQuery(id+"F0.wireOp",EDGE,"E199"),sQuery(id+"F0.wireOp",EDGE,"E200"),sQuery(id+"F0.wireOp",EDGE,"E201"),sQuery(id+"F0.wireOp",EDGE,"E202"),sQuery(id+"F0.wireOp",EDGE,"E203"),sQuery(id+"F0.wireOp",EDGE,"E204"),sQuery(id+"F0.wireOp",EDGE,"E205"),sQuery(id+"F0.wireOp",EDGE,"E206"),sQuery(id+"F0.wireOp",EDGE,"E207"),sQuery(id+"F0.wireOp",EDGE,"E208"),sQuery(id+"F0.wireOp",EDGE,"E209"),sQuery(id+"F0.wireOp",EDGE,"E210"),sQuery(id+"F0.wireOp",EDGE,"E211"),sQuery(id+"F0.wireOp",EDGE,"E212"),sQuery(id+"F0.wireOp",EDGE,"E213"),sQuery(id+"F0.wireOp",EDGE,"E214"),sQuery(id+"F0.wireOp",EDGE,"E215"),sQuery(id+"F0.wireOp",EDGE,"E216"),sQuery(id+"F0.wireOp",EDGE,"E217"),sQuery(id+"F0.wireOp",EDGE,"E218"),sQuery(id+"F0.wireOp",EDGE,"E219"),sQuery(id+"F0.wireOp",EDGE,"E220"),sQuery(id+"F0.wireOp",EDGE,"E221"),sQuery(id+"F0.wireOp",EDGE,"E222"),sQuery(id+"F0.wireOp",EDGE,"E223"),sQuery(id+"F0.wireOp",EDGE,"E224"),sQuery(id+"F0.wireOp",EDGE,"E225"),sQuery(id+"F0.wireOp",EDGE,"E226"),sQuery(id+"F0.wireOp",EDGE,"E227"),sQuery(id+"F0.wireOp",EDGE,"E228"),sQuery(id+"F0.wireOp",EDGE,"E229"),sQuery(id+"F0.wireOp",EDGE,"E230"),sQuery(id+"F0.wireOp",EDGE,"E231"),sQuery(id+"F0.wireOp",EDGE,"E232"),sQuery(id+"F0.wireOp",EDGE,"E233"),sQuery(id+"F0.wireOp",EDGE,"E234"),sQuery(id+"F0.wireOp",EDGE,"E235"),sQuery(id+"F0.wireOp",EDGE,"E236"),sQuery(id+"F0.wireOp",EDGE,"E237"),sQuery(id+"F0.wireOp",EDGE,"E238"),sQuery(id+"F0.wireOp",EDGE,"E239"),sQuery(id+"F0.wireOp",EDGE,"E240"),sQuery(id+"F0.wireOp",EDGE,"E241"),sQuery(id+"F0.wireOp",EDGE,"E242"),sQuery(id+"F0.wireOp",EDGE,"E243"),sQuery(id+"F0.wireOp",EDGE,"E244"),sQuery(id+"F0.wireOp",EDGE,"E245"),sQuery(id+"F0.wireOp",EDGE,"E246"),sQuery(id+"F0.wireOp",EDGE,"E247"),sQuery(id+"F0.wireOp",EDGE,"E248"),sQuery(id+"F0.wireOp",EDGE,"E249"),sQuery(id+"F0.wireOp",EDGE,"E250"),sQuery(id+"F0.wireOp",EDGE,"E251")])],"isStart":false});
            var Q1;
            Q1=makeQuery(id+"F1.opExtrude","CAP_FACE",FACE,{"disambiguationData":[OSD([sQuery(id+"F0.wireOp",EDGE,"E0"),sQuery(id+"F0.wireOp",EDGE,"E1"),sQuery(id+"F0.wireOp",EDGE,"E2"),sQuery(id+"F0.wireOp",EDGE,"E3"),sQuery(id+"F0.wireOp",EDGE,"E4"),sQuery(id+"F0.wireOp",EDGE,"E5"),sQuery(id+"F0.wireOp",EDGE,"E6"),sQuery(id+"F0.wireOp",EDGE,"E7"),sQuery(id+"F0.wireOp",EDGE,"E8"),sQuery(id+"F0.wireOp",EDGE,"E9"),sQuery(id+"F0.wireOp",EDGE,"E10"),sQuery(id+"F0.wireOp",EDGE,"E11"),sQuery(id+"F0.wireOp",EDGE,"E12"),sQuery(id+"F0.wireOp",EDGE,"E13"),sQuery(id+"F0.wireOp",EDGE,"E14"),sQuery(id+"F0.wireOp",EDGE,"E15"),sQuery(id+"F0.wireOp",EDGE,"E16"),sQuery(id+"F0.wireOp",EDGE,"E17"),sQuery(id+"F0.wireOp",EDGE,"E18"),sQuery(id+"F0.wireOp",EDGE,"E19"),sQuery(id+"F0.wireOp",EDGE,"E20"),sQuery(id+"F0.wireOp",EDGE,"E21"),sQuery(id+"F0.wireOp",EDGE,"E22"),sQuery(id+"F0.wireOp",EDGE,"E23"),sQuery(id+"F0.wireOp",EDGE,"E24"),sQuery(id+"F0.wireOp",EDGE,"E25"),sQuery(id+"F0.wireOp",EDGE,"E26"),sQuery(id+"F0.wireOp",EDGE,"E27"),sQuery(id+"F0.wireOp",EDGE,"E28"),sQuery(id+"F0.wireOp",EDGE,"E29"),sQuery(id+"F0.wireOp",EDGE,"E30"),sQuery(id+"F0.wireOp",EDGE,"E31"),sQuery(id+"F0.wireOp",EDGE,"E32"),sQuery(id+"F0.wireOp",EDGE,"E33"),sQuery(id+"F0.wireOp",EDGE,"E34"),sQuery(id+"F0.wireOp",EDGE,"E35"),sQuery(id+"F0.wireOp",EDGE,"E36"),sQuery(id+"F0.wireOp",EDGE,"E37"),sQuery(id+"F0.wireOp",EDGE,"E38"),sQuery(id+"F0.wireOp",EDGE,"E39"),sQuery(id+"F0.wireOp",EDGE,"E40"),sQuery(id+"F0.wireOp",EDGE,"E41"),sQuery(id+"F0.wireOp",EDGE,"E42"),sQuery(id+"F0.wireOp",EDGE,"E43"),sQuery(id+"F0.wireOp",EDGE,"E44"),sQuery(id+"F0.wireOp",EDGE,"E45"),sQuery(id+"F0.wireOp",EDGE,"E46"),sQuery(id+"F0.wireOp",EDGE,"E47"),sQuery(id+"F0.wireOp",EDGE,"E48"),sQuery(id+"F0.wireOp",EDGE,"E49"),sQuery(id+"F0.wireOp",EDGE,"E50"),sQuery(id+"F0.wireOp",EDGE,"E51"),sQuery(id+"F0.wireOp",EDGE,"E52"),sQuery(id+"F0.wireOp",EDGE,"E53"),sQuery(id+"F0.wireOp",EDGE,"E54"),sQuery(id+"F0.wireOp",EDGE,"E55"),sQuery(id+"F0.wireOp",EDGE,"E56"),sQuery(id+"F0.wireOp",EDGE,"E57"),sQuery(id+"F0.wireOp",EDGE,"E58"),sQuery(id+"F0.wireOp",EDGE,"E59"),sQuery(id+"F0.wireOp",EDGE,"E60"),sQuery(id+"F0.wireOp",EDGE,"E61"),sQuery(id+"F0.wireOp",EDGE,"E62"),sQuery(id+"F0.wireOp",EDGE,"E63"),sQuery(id+"F0.wireOp",EDGE,"E64"),sQuery(id+"F0.wireOp",EDGE,"E65"),sQuery(id+"F0.wireOp",EDGE,"E66"),sQuery(id+"F0.wireOp",EDGE,"E67"),sQuery(id+"F0.wireOp",EDGE,"E68"),sQuery(id+"F0.wireOp",EDGE,"E69"),sQuery(id+"F0.wireOp",EDGE,"E70"),sQuery(id+"F0.wireOp",EDGE,"E71"),sQuery(id+"F0.wireOp",EDGE,"E72"),sQuery(id+"F0.wireOp",EDGE,"E73"),sQuery(id+"F0.wireOp",EDGE,"E74"),sQuery(id+"F0.wireOp",EDGE,"E75"),sQuery(id+"F0.wireOp",EDGE,"E76"),sQuery(id+"F0.wireOp",EDGE,"E77"),sQuery(id+"F0.wireOp",EDGE,"E78"),sQuery(id+"F0.wireOp",EDGE,"E79"),sQuery(id+"F0.wireOp",EDGE,"E80"),sQuery(id+"F0.wireOp",EDGE,"E81"),sQuery(id+"F0.wireOp",EDGE,"E82"),sQuery(id+"F0.wireOp",EDGE,"E83"),sQuery(id+"F0.wireOp",EDGE,"E84"),sQuery(id+"F0.wireOp",EDGE,"E85"),sQuery(id+"F0.wireOp",EDGE,"E86"),sQuery(id+"F0.wireOp",EDGE,"E87"),sQuery(id+"F0.wireOp",EDGE,"E88"),sQuery(id+"F0.wireOp",EDGE,"E89"),sQuery(id+"F0.wireOp",EDGE,"E90"),sQuery(id+"F0.wireOp",EDGE,"E91"),sQuery(id+"F0.wireOp",EDGE,"E92"),sQuery(id+"F0.wireOp",EDGE,"E93"),sQuery(id+"F0.wireOp",EDGE,"E94"),sQuery(id+"F0.wireOp",EDGE,"E95"),sQuery(id+"F0.wireOp",EDGE,"E96"),sQuery(id+"F0.wireOp",EDGE,"E97"),sQuery(id+"F0.wireOp",EDGE,"E98"),sQuery(id+"F0.wireOp",EDGE,"E99"),sQuery(id+"F0.wireOp",EDGE,"E100"),sQuery(id+"F0.wireOp",EDGE,"E101"),sQuery(id+"F0.wireOp",EDGE,"E102"),sQuery(id+"F0.wireOp",EDGE,"E103"),sQuery(id+"F0.wireOp",EDGE,"E104"),sQuery(id+"F0.wireOp",EDGE,"E105"),sQuery(id+"F0.wireOp",EDGE,"E106"),sQuery(id+"F0.wireOp",EDGE,"E107"),sQuery(id+"F0.wireOp",EDGE,"E108"),sQuery(id+"F0.wireOp",EDGE,"E109"),sQuery(id+"F0.wireOp",EDGE,"E110"),sQuery(id+"F0.wireOp",EDGE,"E111"),sQuery(id+"F0.wireOp",EDGE,"E112"),sQuery(id+"F0.wireOp",EDGE,"E113"),sQuery(id+"F0.wireOp",EDGE,"E114"),sQuery(id+"F0.wireOp",EDGE,"E115"),sQuery(id+"F0.wireOp",EDGE,"E116"),sQuery(id+"F0.wireOp",EDGE,"E117"),sQuery(id+"F0.wireOp",EDGE,"E118"),sQuery(id+"F0.wireOp",EDGE,"E119"),sQuery(id+"F0.wireOp",EDGE,"E120"),sQuery(id+"F0.wireOp",EDGE,"E121"),sQuery(id+"F0.wireOp",EDGE,"E122"),sQuery(id+"F0.wireOp",EDGE,"E123"),sQuery(id+"F0.wireOp",EDGE,"E124"),sQuery(id+"F0.wireOp",EDGE,"E125"),sQuery(id+"F0.wireOp",EDGE,"E126"),sQuery(id+"F0.wireOp",EDGE,"E127"),sQuery(id+"F0.wireOp",EDGE,"E128"),sQuery(id+"F0.wireOp",EDGE,"E129"),sQuery(id+"F0.wireOp",EDGE,"E130"),sQuery(id+"F0.wireOp",EDGE,"E131"),sQuery(id+"F0.wireOp",EDGE,"E132"),sQuery(id+"F0.wireOp",EDGE,"E133"),sQuery(id+"F0.wireOp",EDGE,"E134"),sQuery(id+"F0.wireOp",EDGE,"E135"),sQuery(id+"F0.wireOp",EDGE,"E136"),sQuery(id+"F0.wireOp",EDGE,"E137"),sQuery(id+"F0.wireOp",EDGE,"E138"),sQuery(id+"F0.wireOp",EDGE,"E139"),sQuery(id+"F0.wireOp",EDGE,"E140"),sQuery(id+"F0.wireOp",EDGE,"E141"),sQuery(id+"F0.wireOp",EDGE,"E142"),sQuery(id+"F0.wireOp",EDGE,"E143"),sQuery(id+"F0.wireOp",EDGE,"E144"),sQuery(id+"F0.wireOp",EDGE,"E145"),sQuery(id+"F0.wireOp",EDGE,"E146"),sQuery(id+"F0.wireOp",EDGE,"E147"),sQuery(id+"F0.wireOp",EDGE,"E148"),sQuery(id+"F0.wireOp",EDGE,"E149"),sQuery(id+"F0.wireOp",EDGE,"E150"),sQuery(id+"F0.wireOp",EDGE,"E151"),sQuery(id+"F0.wireOp",EDGE,"E152"),sQuery(id+"F0.wireOp",EDGE,"E153"),sQuery(id+"F0.wireOp",EDGE,"E154"),sQuery(id+"F0.wireOp",EDGE,"E155"),sQuery(id+"F0.wireOp",EDGE,"E156"),sQuery(id+"F0.wireOp",EDGE,"E157"),sQuery(id+"F0.wireOp",EDGE,"E158"),sQuery(id+"F0.wireOp",EDGE,"E159"),sQuery(id+"F0.wireOp",EDGE,"E160"),sQuery(id+"F0.wireOp",EDGE,"E161"),sQuery(id+"F0.wireOp",EDGE,"E162"),sQuery(id+"F0.wireOp",EDGE,"E163"),sQuery(id+"F0.wireOp",EDGE,"E164"),sQuery(id+"F0.wireOp",EDGE,"E165"),sQuery(id+"F0.wireOp",EDGE,"E166"),sQuery(id+"F0.wireOp",EDGE,"E167"),sQuery(id+"F0.wireOp",EDGE,"E168"),sQuery(id+"F0.wireOp",EDGE,"E169"),sQuery(id+"F0.wireOp",EDGE,"E170"),sQuery(id+"F0.wireOp",EDGE,"E171"),sQuery(id+"F0.wireOp",EDGE,"E172"),sQuery(id+"F0.wireOp",EDGE,"E173"),sQuery(id+"F0.wireOp",EDGE,"E174"),sQuery(id+"F0.wireOp",EDGE,"E175"),sQuery(id+"F0.wireOp",EDGE,"E176"),sQuery(id+"F0.wireOp",EDGE,"E177"),sQuery(id+"F0.wireOp",EDGE,"E178"),sQuery(id+"F0.wireOp",EDGE,"E179"),sQuery(id+"F0.wireOp",EDGE,"E180"),sQuery(id+"F0.wireOp",EDGE,"E181"),sQuery(id+"F0.wireOp",EDGE,"E182"),sQuery(id+"F0.wireOp",EDGE,"E183"),sQuery(id+"F0.wireOp",EDGE,"E184"),sQuery(id+"F0.wireOp",EDGE,"E185"),sQuery(id+"F0.wireOp",EDGE,"E186"),sQuery(id+"F0.wireOp",EDGE,"E187"),sQuery(id+"F0.wireOp",EDGE,"E188"),sQuery(id+"F0.wireOp",EDGE,"E189"),sQuery(id+"F0.wireOp",EDGE,"E190"),sQuery(id+"F0.wireOp",EDGE,"E191"),sQuery(id+"F0.wireOp",EDGE,"E192"),sQuery(id+"F0.wireOp",EDGE,"E193"),sQuery(id+"F0.wireOp",EDGE,"E194"),sQuery(id+"F0.wireOp",EDGE,"E195"),sQuery(id+"F0.wireOp",EDGE,"E196"),sQuery(id+"F0.wireOp",EDGE,"E197"),sQuery(id+"F0.wireOp",EDGE,"E198"),sQuery(id+"F0.wireOp",EDGE,"E199"),sQuery(id+"F0.wireOp",EDGE,"E200"),sQuery(id+"F0.wireOp",EDGE,"E201"),sQuery(id+"F0.wireOp",EDGE,"E202"),sQuery(id+"F0.wireOp",EDGE,"E203"),sQuery(id+"F0.wireOp",EDGE,"E204"),sQuery(id+"F0.wireOp",EDGE,"E205"),sQuery(id+"F0.wireOp",EDGE,"E206"),sQuery(id+"F0.wireOp",EDGE,"E207"),sQuery(id+"F0.wireOp",EDGE,"E208"),sQuery(id+"F0.wireOp",EDGE,"E209"),sQuery(id+"F0.wireOp",EDGE,"E210"),sQuery(id+"F0.wireOp",EDGE,"E211"),sQuery(id+"F0.wireOp",EDGE,"E212"),sQuery(id+"F0.wireOp",EDGE,"E213"),sQuery(id+"F0.wireOp",EDGE,"E214"),sQuery(id+"F0.wireOp",EDGE,"E215"),sQuery(id+"F0.wireOp",EDGE,"E216"),sQuery(id+"F0.wireOp",EDGE,"E217"),sQuery(id+"F0.wireOp",EDGE,"E218"),sQuery(id+"F0.wireOp",EDGE,"E219"),sQuery(id+"F0.wireOp",EDGE,"E220"),sQuery(id+"F0.wireOp",EDGE,"E221"),sQuery(id+"F0.wireOp",EDGE,"E222"),sQuery(id+"F0.wireOp",EDGE,"E223"),sQuery(id+"F0.wireOp",EDGE,"E224"),sQuery(id+"F0.wireOp",EDGE,"E225"),sQuery(id+"F0.wireOp",EDGE,"E226"),sQuery(id+"F0.wireOp",EDGE,"E227"),sQuery(id+"F0.wireOp",EDGE,"E228"),sQuery(id+"F0.wireOp",EDGE,"E229"),sQuery(id+"F0.wireOp",EDGE,"E230"),sQuery(id+"F0.wireOp",EDGE,"E231"),sQuery(id+"F0.wireOp",EDGE,"E232"),sQuery(id+"F0.wireOp",EDGE,"E233"),sQuery(id+"F0.wireOp",EDGE,"E234"),sQuery(id+"F0.wireOp",EDGE,"E235"),sQuery(id+"F0.wireOp",EDGE,"E236"),sQuery(id+"F0.wireOp",EDGE,"E237"),sQuery(id+"F0.wireOp",EDGE,"E238"),sQuery(id+"F0.wireOp",EDGE,"E239"),sQuery(id+"F0.wireOp",EDGE,"E240"),sQuery(id+"F0.wireOp",EDGE,"E241"),sQuery(id+"F0.wireOp",EDGE,"E242"),sQuery(id+"F0.wireOp",EDGE,"E243"),sQuery(id+"F0.wireOp",EDGE,"E244"),sQuery(id+"F0.wireOp",EDGE,"E245"),sQuery(id+"F0.wireOp",EDGE,"E246"),sQuery(id+"F0.wireOp",EDGE,"E247"),sQuery(id+"F0.wireOp",EDGE,"E248"),sQuery(id+"F0.wireOp",EDGE,"E249"),sQuery(id+"F0.wireOp",EDGE,"E250"),sQuery(id+"F0.wireOp",EDGE,"E251")])],"isStart":true});
            fillet(context, id + "F2", {"entities" : qUnion([Q0, Q1]), "radius" : 0.3 * mm, "tangentPropagation" : true, "allowEdgeOverflow" : false});
        }
    });
